# Revit family: Deca_Base para registro de gaveta_Base_4509.000
name_source: partatom
category: Pipe Accessories
units: mm (PartAtom-declared; Revit-internal decimal feet)

## family parameters
Cut with Voids When Loaded = No
Host = Face
Part Type = Normal
Round Connector Dimension = Use Radius
Shared = No

## types (1)
- 4509.202_Bruto_DN20
    Acompanha o Produto = Sem acompanhamento
    Aprovado por = quattroD
    Atendimento ao Cliente = 0800-0117073
    Categoria = -
    Composição Anel Vedação = -
    Composição Assento = -
    Composição Básica = Liga de Cobre (bronze e latão),Plásticos de Engenharia,Elastômeros
    Composição Componente = -
    Consumo = -
    Cor Interna = -
    Cor Principal = -
    Cor Secundária = -
    Cores Componente = -
    Criado por = quattroD
    Código Pai = 4509.202
    Default Elevation = 1.8 m
    Diâmetro Água Fria = 0.02 m
    Informações Complementares = -
    Itens de Instalação = -
    Linha = sem linha
    Manufacturer = Deca
    Material = Deca_Bruto
    Model = 4509.202
    Norma = -
    Peso Líquido (Kg) = 0
    Pressão máx. funcionamento = -
    Pressão mín. Aquec. Acúmulo = -
    Pressão mín. Aquec. Passagem = -
    Pressão mín. funcionamento = -
    Raio Água Fria = 0.01 m
    Saída de Esgoto = -
    Segmento = Básicos
    Tipo de dispositivo economizador = -
    Tipo de mecanismo utilizado = -
    Tipo de rosca de entrada = -
    Tipo de rosca de saída = -
    URL = www.deca.com.br
    Vazão na Pressão máx. (L/min) = -
    Vazão na Pressão mín. (L/min) = -

## geometry (parser evidence)
native form markers: Sweep x2
no freeform markers — native parametric forms only
